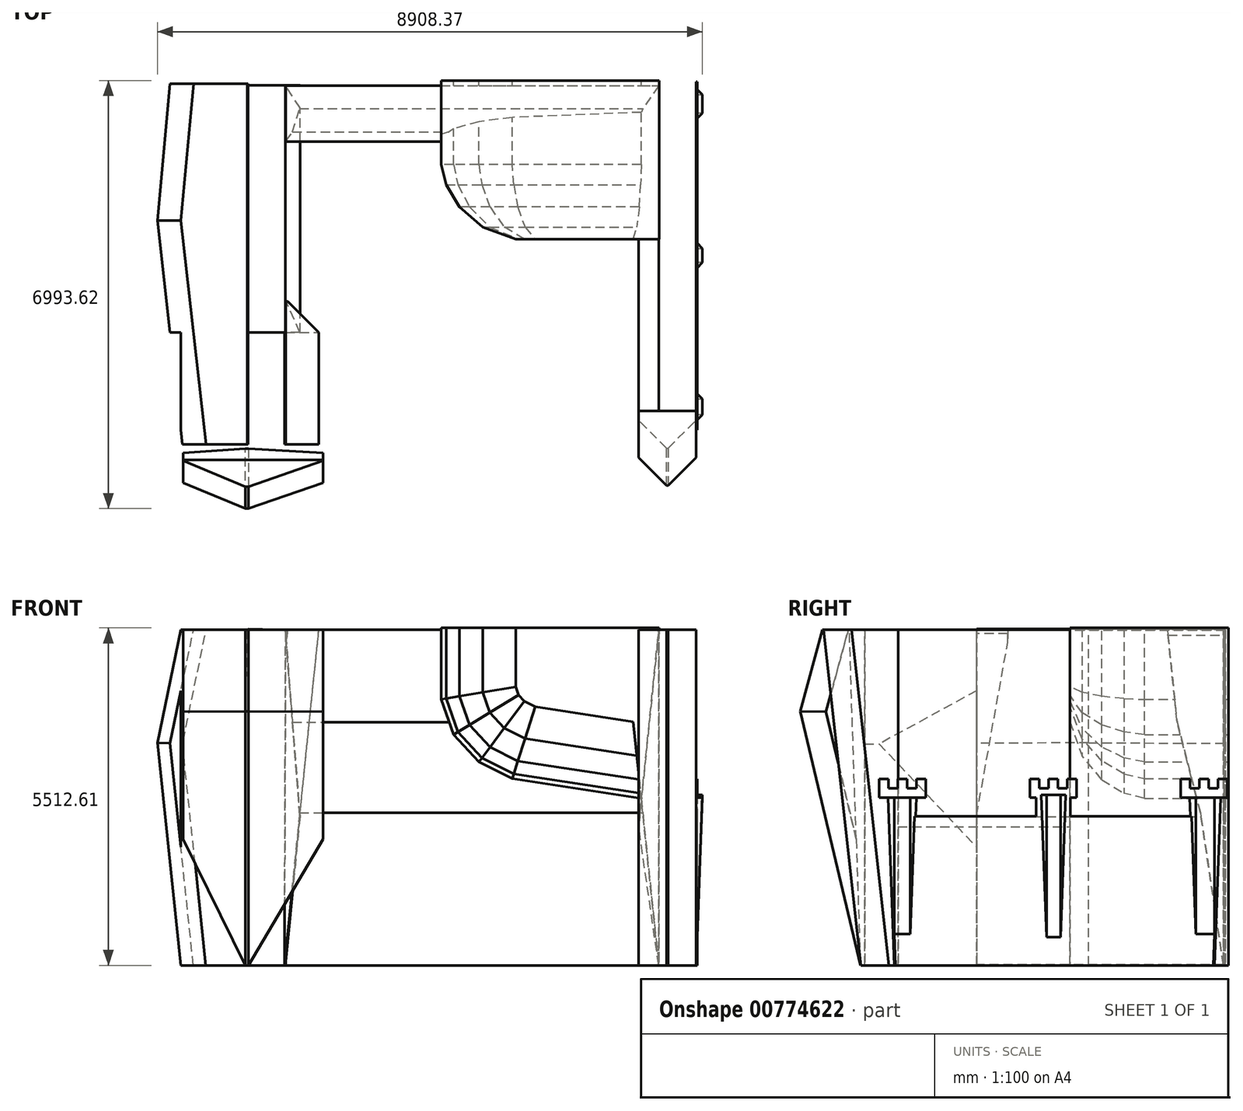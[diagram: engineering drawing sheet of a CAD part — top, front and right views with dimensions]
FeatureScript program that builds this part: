
annotation { "Feature Type Name" : "Feature", "Feature Type Description" : "" }
export const myFeature = defineFeature(function(context is Context, id is Id, definition is map)
    precondition{}
    {
        {
            var Q0;
            Q0=qCreatedBy(makeId("Right.planeOp"),FACE);
            var sketch = newSketch(context, id + "F0", { "sketchPlane" : qUnion([Q0])});
            skLineSegment(sketch, "E0", {"start": v(336.19, 0) * mm, "end": v(336.19, 2438.4) * mm});
            skLineSegment(sketch, "E1", {"start": v(336.19, 2438.4) * mm, "end": v(-5150.21, 2438.4) * mm});
            skLineSegment(sketch, "E2", {"start": v(-5150.21, 2438.4) * mm, "end": v(-5150.21, 0) * mm});
            skLineSegment(sketch, "E3", {"start": v(-5150.21, 0) * mm, "end": v(336.19, 0) * mm});
            skLineSegment(sketch, "E4", {"start": v(-5150.21, 2438.4) * mm, "end": v(-5150.21, 2743.2) * mm});
            skLineSegment(sketch, "E5", {"start": v(-5150.21, 2743.2) * mm, "end": v(-5251.81, 2743.2) * mm});
            skLineSegment(sketch, "E6", {"start": v(-5251.81, 2743.2) * mm, "end": v(-5251.81, 3048) * mm});
            skLineSegment(sketch, "E7", {"start": v(-5251.81, 3048) * mm, "end": v(-5099.41, 3048) * mm});
            skLineSegment(sketch, "E8", {"start": v(-5099.41, 3048) * mm, "end": v(-5099.41, 2895.6) * mm});
            skLineSegment(sketch, "E9", {"start": v(-5099.41, 2895.6) * mm, "end": v(-4947.01, 2895.6) * mm});
            skLineSegment(sketch, "E10", {"start": v(-4947.01, 2895.6) * mm, "end": v(-4947.01, 3048) * mm});
            skLineSegment(sketch, "E11", {"start": v(-4947.01, 3048) * mm, "end": v(-4794.61, 3048) * mm});
            skLineSegment(sketch, "E12", {"start": v(-4794.61, 3048) * mm, "end": v(-4794.61, 2895.6) * mm});
            skLineSegment(sketch, "E13", {"start": v(-4794.61, 2895.6) * mm, "end": v(-4642.21, 2895.6) * mm});
            skLineSegment(sketch, "E14", {"start": v(-4642.21, 2895.6) * mm, "end": v(-4642.21, 3048) * mm});
            skLineSegment(sketch, "E15", {"start": v(-4642.21, 3048) * mm, "end": v(-4489.81, 3048) * mm});
            skLineSegment(sketch, "E16", {"start": v(-4489.81, 3048) * mm, "end": v(-4489.81, 2743.2) * mm});
            skLineSegment(sketch, "E17", {"start": v(-4489.81, 2743.2) * mm, "end": v(-4591.41, 2743.2) * mm});
            skLineSegment(sketch, "E18", {"start": v(-4591.41, 2743.2) * mm, "end": v(-4591.41, 2438.4) * mm});
            skLineSegment(sketch, "E19", {"start": v(-4591.41, 2438.4) * mm, "end": v(-2686.41, 2438.4) * mm});
            skLineSegment(sketch, "E20", {"start": v(336.19, 2438.4) * mm, "end": v(336.19, 2743.2) * mm});
            skLineSegment(sketch, "E21", {"start": v(336.19, 2743.2) * mm, "end": v(437.79, 2743.2) * mm});
            skLineSegment(sketch, "E22", {"start": v(437.79, 2743.2) * mm, "end": v(437.79, 3048) * mm});
            skLineSegment(sketch, "E23", {"start": v(437.79, 3048) * mm, "end": v(285.39, 3048) * mm});
            skLineSegment(sketch, "E24", {"start": v(285.39, 3048) * mm, "end": v(285.39, 2895.6) * mm});
            skLineSegment(sketch, "E25", {"start": v(285.39, 2895.6) * mm, "end": v(132.99, 2895.6) * mm});
            skLineSegment(sketch, "E26", {"start": v(132.99, 2895.6) * mm, "end": v(132.99, 3048) * mm});
            skLineSegment(sketch, "E27", {"start": v(132.99, 3048) * mm, "end": v(-19.41, 3048) * mm});
            skLineSegment(sketch, "E28", {"start": v(-19.41, 3048) * mm, "end": v(-19.41, 2895.6) * mm});
            skLineSegment(sketch, "E29", {"start": v(-19.41, 2895.6) * mm, "end": v(-171.81, 2895.6) * mm});
            skLineSegment(sketch, "E30", {"start": v(-171.81, 2895.6) * mm, "end": v(-171.81, 3048) * mm});
            skLineSegment(sketch, "E31", {"start": v(-171.81, 3048) * mm, "end": v(-324.21, 3048) * mm});
            skLineSegment(sketch, "E32", {"start": v(-324.21, 3048) * mm, "end": v(-324.21, 2743.2) * mm});
            skLineSegment(sketch, "E33", {"start": v(-324.21, 2743.2) * mm, "end": v(-222.61, 2743.2) * mm});
            skLineSegment(sketch, "E34", {"start": v(-222.61, 2743.2) * mm, "end": v(-222.61, 2438.4) * mm});
            skLineSegment(sketch, "E35", {"start": v(-222.61, 2438.4) * mm, "end": v(-2127.61, 2438.4) * mm});
            skLineSegment(sketch, "E36", {"start": v(-2686.41, 2438.4) * mm, "end": v(-2686.41, 2743.2) * mm});
            skLineSegment(sketch, "E37", {"start": v(-2686.41, 2743.2) * mm, "end": v(-2788.01, 2743.2) * mm});
            skLineSegment(sketch, "E38", {"start": v(-2788.01, 2743.2) * mm, "end": v(-2788.01, 3048) * mm});
            skLineSegment(sketch, "E39", {"start": v(-2788.01, 3048) * mm, "end": v(-2635.61, 3048) * mm});
            skLineSegment(sketch, "E40", {"start": v(-2635.61, 3048) * mm, "end": v(-2635.61, 2895.6) * mm});
            skLineSegment(sketch, "E41", {"start": v(-2635.61, 2895.6) * mm, "end": v(-2483.21, 2895.6) * mm});
            skLineSegment(sketch, "E42", {"start": v(-2483.21, 2895.6) * mm, "end": v(-2483.21, 3048) * mm});
            skLineSegment(sketch, "E43", {"start": v(-2483.21, 3048) * mm, "end": v(-2330.81, 3048) * mm});
            skLineSegment(sketch, "E44", {"start": v(-2330.81, 3048) * mm, "end": v(-2330.81, 2895.6) * mm});
            skLineSegment(sketch, "E45", {"start": v(-2330.81, 2895.6) * mm, "end": v(-2178.41, 2895.6) * mm});
            skLineSegment(sketch, "E46", {"start": v(-2178.41, 2895.6) * mm, "end": v(-2178.41, 3048) * mm});
            skLineSegment(sketch, "E47", {"start": v(-2178.41, 3048) * mm, "end": v(-2026.01, 3048) * mm});
            skLineSegment(sketch, "E48", {"start": v(-2026.01, 3048) * mm, "end": v(-2026.01, 2743.2) * mm});
            skLineSegment(sketch, "E49", {"start": v(-2026.01, 2743.2) * mm, "end": v(-2127.61, 2743.2) * mm});
            skLineSegment(sketch, "E50", {"start": v(-2127.61, 2743.2) * mm, "end": v(-2127.61, 2438.4) * mm});
            skLineSegment(sketch, "E51", {"start": v(-2127.61, 2438.4) * mm, "end": v(-2127.61, 2438.4) * mm});
            skLineSegment(sketch, "E52", {"start": v(-2127.61, 2438.4) * mm, "end": v(-2686.41, 2438.4) * mm});
            skSolve(sketch);
        }
        {
            var Q0;
            Q0 = qSketchRegion(id + "F0", true);
            extrude(context, id + "F1", {"entities" : qUnion([Q0]), "depth" : 19.05 * mm, "offsetDistance" : 25.4 * mm});
        }
        {
            var Q0;
            Q0=qCreatedBy(makeId("Front.planeOp"),FACE);
            var sketch = newSketch(context, id + "F2", { "sketchPlane" : qUnion([Q0])});
            skLineSegment(sketch, "E53", {"start": v(0, 0) * mm, "end": v(0, 2743.2) * mm});
            skLineSegment(sketch, "E54", {"start": v(0, 2743.2) * mm, "end": v(101.6, 2743.2) * mm});
            skLineSegment(sketch, "E55", {"start": v(101.6, 2743.2) * mm, "end": v(0, 0) * mm});
            skSolve(sketch);
        }
        {
            var Q0;
            Q0 = qSketchRegion(id + "F2", true);
            extrude(context, id + "F3", {"entities" : qUnion([Q0]), "operationType" : NewBodyOperationType.ADD, "depth" : 228.6 * mm, "offsetDistance" : 25.4 * mm, "hasSecondDirection" : true, "secondDirectionOppositeDirection" : true, "secondDirectionDepth" : 381 * mm});
        }
        {
            var Q0;
            Q0=makeQuery(id+"F3.opExtrude","CAP_EDGE",EDGE,{"disambiguationData":[OSD([sQuery(id+"F2.wireOp",EDGE,"E55")])],"isStart":false});
            var Q1;
            Q1=makeQuery(id+"F3.opExtrude","CAP_EDGE",EDGE,{"disambiguationData":[OSD([sQuery(id+"F2.wireOp",EDGE,"E55")])],"isStart":true});
            chamfer(context, id + "F4", {"entities" : qUnion([Q0, Q1]), "width" : 152.4 * mm, "tangentPropagation" : true});
        }
        {
            var Q0;
            Q0=qCreatedBy(makeId("Front.planeOp"),FACE);
            var sketch = newSketch(context, id + "F5", { "sketchPlane" : qUnion([Q0])});
            skLineSegment(sketch, "E56", {"start": v(3.6, 45.14) * mm, "end": v(3.6, 2788.34) * mm});
            skLineSegment(sketch, "E57", {"start": v(3.6, 2788.34) * mm, "end": v(105.2, 2788.34) * mm});
            skLineSegment(sketch, "E58", {"start": v(105.2, 2788.34) * mm, "end": v(3.6, 45.14) * mm});
            skSolve(sketch);
        }
        {
            var Q0;
            Q0 = qSketchRegion(id + "F5", true);
            extrude(context, id + "F6", {"entities" : qUnion([Q0]), "operationType" : NewBodyOperationType.ADD, "depth" : 2667 * mm, "offsetDistance" : 25.4 * mm, "hasSecondDirection" : true, "secondDirectionOppositeDirection" : false, "secondDirectionDepth" : 2133.6 * mm});
        }
        {
            var Q0;
            Q0=makeQuery(id+"F6.opExtrude","CAP_EDGE",EDGE,{"disambiguationData":[OSD([sQuery(id+"F5.wireOp",EDGE,"E58")])],"isStart":true});
            var Q1;
            Q1=makeQuery(id+"F6.opExtrude","CAP_EDGE",EDGE,{"disambiguationData":[OSD([sQuery(id+"F5.wireOp",EDGE,"E58")])],"isStart":false});
            chamfer(context, id + "F7", {"entities" : qUnion([Q0, Q1]), "width" : 152.4 * mm, "tangentPropagation" : true});
        }
        {
            var Q0;
            Q0=qCreatedBy(makeId("Front.planeOp"),FACE);
            var sketch = newSketch(context, id + "F8", { "sketchPlane" : qUnion([Q0])});
            skLineSegment(sketch, "E59", {"start": v(0, 0) * mm, "end": v(0, 2743.2) * mm});
            skLineSegment(sketch, "E60", {"start": v(0, 2743.2) * mm, "end": v(101.6, 2743.2) * mm});
            skLineSegment(sketch, "E61", {"start": v(101.6, 2743.2) * mm, "end": v(0, 0) * mm});
            skSolve(sketch);
        }
        {
            var Q0;
            Q0 = qSketchRegion(id + "F8", true);
            extrude(context, id + "F9", {"entities" : qUnion([Q0]), "operationType" : NewBodyOperationType.ADD, "depth" : 5156.2 * mm, "offsetDistance" : 25.4 * mm, "hasSecondDirection" : true, "secondDirectionOppositeDirection" : false, "secondDirectionDepth" : 4589.78 * mm});
        }
        {
            var Q0;
            Q0=makeQuery(id+"F9.opExtrude","CAP_EDGE",EDGE,{"disambiguationData":[OSD([sQuery(id+"F8.wireOp",EDGE,"E61")])],"isStart":false});
            var Q1;
            Q1=makeQuery(id+"F9.opExtrude","CAP_EDGE",EDGE,{"disambiguationData":[OSD([sQuery(id+"F8.wireOp",EDGE,"E61")])],"isStart":true});
            chamfer(context, id + "F10", {"entities" : qUnion([Q0, Q1]), "width" : 152.4 * mm, "tangentPropagation" : true});
        }
        {
            var Q0;
            Q0=qCreatedBy(makeId("Front.planeOp"),FACE);
            var sketch = newSketch(context, id + "F11", { "sketchPlane" : qUnion([Q0])});
            skLineSegment(sketch, "E62", {"start": v(0, 0) * mm, "end": v(-609.6, 0) * mm});
            skLineSegment(sketch, "E63", {"start": v(-609.6, 0) * mm, "end": v(-609.6, 5486.4) * mm});
            skLineSegment(sketch, "E64", {"start": v(-609.6, 0) * mm, "end": v(-938.3, 2262.25) * mm});
            skLineSegment(sketch, "E65", {"start": v(-938.3, 2262.25) * mm, "end": v(-609.6, 5486.4) * mm});
            skSolve(sketch);
        }
        {
            var Q0;
            Q0 = qSketchRegion(id + "F11", true);
            extrude(context, id + "F12", {"entities" : qUnion([Q0]), "depth" : 4978.4 * mm, "offsetDistance" : 25.4 * mm, "hasSecondDirection" : true, "secondDirectionOppositeDirection" : false, "secondDirectionDepth" : 2133.6 * mm});
        }
        {
            var Q0;
            Q0=qCreatedBy(makeId("Front.planeOp"),FACE);
            var sketch = newSketch(context, id + "F13", { "sketchPlane" : qUnion([Q0])});
            skLineSegment(sketch, "E66", {"start": v(-608.8, 0) * mm, "end": v(-895.68, 2728.16) * mm});
            skLineSegment(sketch, "E67", {"start": v(-895.68, 2728.16) * mm, "end": v(-3004.94, 3049.56) * mm});
            skLineSegment(sketch, "E68", {"start": v(-3004.94, 3049.56) * mm, "end": v(-3549.82, 3322.9) * mm});
            skLineSegment(sketch, "E69", {"start": v(-3549.82, 3322.9) * mm, "end": v(-3964.79, 3769.46) * mm});
            skLineSegment(sketch, "E70", {"start": v(-3964.79, 3769.46) * mm, "end": v(-4167.95, 4344.2) * mm});
            skLineSegment(sketch, "E71", {"start": v(-4167.95, 4344.2) * mm, "end": v(-4167.95, 5512.6) * mm});
            skLineSegment(sketch, "E72", {"start": v(-4167.95, 5512.6) * mm, "end": v(-605.67, 5512.6) * mm});
            skLineSegment(sketch, "E73", {"start": v(-605.67, 5512.6) * mm, "end": v(-608.8, 0) * mm});
            skSolve(sketch);
        }
        {
            var Q0;
            Q0 = qSketchRegion(id + "F13", true);
            extrude(context, id + "F14", {"entities" : qUnion([Q0]), "operationType" : NewBodyOperationType.ADD, "depth" : 2133.6 * mm, "offsetDistance" : 25.4 * mm, "hasSecondDirection" : true, "secondDirectionOppositeDirection" : true, "secondDirectionDepth" : 457.2 * mm});
        }
        {
            var Q0;
            Q0=makeQuery(id+"F14.opExtrude","CAP_EDGE",EDGE,{"disambiguationData":[OSD([sQuery(id+"F13.wireOp",EDGE,"E70")])],"isStart":false});
            var Q1;
            Q1=makeQuery(id+"F14.opExtrude","CAP_EDGE",EDGE,{"disambiguationData":[OSD([sQuery(id+"F13.wireOp",EDGE,"E71")])],"isStart":false});
            var Q2;
            Q2=makeQuery(id+"F14.opExtrude","CAP_EDGE",EDGE,{"disambiguationData":[OSD([sQuery(id+"F13.wireOp",EDGE,"E69")])],"isStart":false});
            var Q3;
            Q3=makeQuery(id+"F14.opExtrude","CAP_EDGE",EDGE,{"disambiguationData":[OSD([sQuery(id+"F13.wireOp",EDGE,"E67")])],"isStart":false});
            var Q4;
            Q4=makeQuery(id+"F14.opExtrude","CAP_EDGE",EDGE,{"disambiguationData":[OSD([sQuery(id+"F13.wireOp",EDGE,"E68")])],"isStart":false});
            chamfer(context, id + "F15", {"entities" : qUnion([Q0, Q1, Q2, Q3, Q4]), "chamferType" : ChamferType.TWO_OFFSETS, "width1" : 1219.2 * mm, "oppositeDirection" : false, "width2" : 304.8 * mm, "tangentPropagation" : true});
        }
        {
            var Q0;
            {var subQ0=sQuery(id+"F13.wireOp",EDGE,"E71");Q0=makeQuery(id+"F15.opChamfer","BLEND_EDGE",EDGE,{"blendedFrom":[makeQuery(id+"F14.opExtrude","CAP_EDGE",EDGE,{"disambiguationData":[OSD([subQ0])],"isStart":false}),makeQuery(id+"F14.opExtrude","CAP_FACE",FACE,{"disambiguationData":[OSD([sQuery(id+"F13.wireOp",EDGE,"E66"),sQuery(id+"F13.wireOp",EDGE,"E67"),sQuery(id+"F13.wireOp",EDGE,"E68"),sQuery(id+"F13.wireOp",EDGE,"E69"),sQuery(id+"F13.wireOp",EDGE,"E70"),subQ0,sQuery(id+"F13.wireOp",EDGE,"E72"),sQuery(id+"F13.wireOp",EDGE,"E73")])],"isStart":false})],"blendedInto":[makeQuery(id+"F14.opExtrude","CAP_FACE",FACE,{"disambiguationData":[OSD([sQuery(id+"F13.wireOp",EDGE,"E66"),sQuery(id+"F13.wireOp",EDGE,"E67"),sQuery(id+"F13.wireOp",EDGE,"E68"),sQuery(id+"F13.wireOp",EDGE,"E69"),sQuery(id+"F13.wireOp",EDGE,"E70"),subQ0,sQuery(id+"F13.wireOp",EDGE,"E72"),sQuery(id+"F13.wireOp",EDGE,"E73")])],"isStart":false})]});}
            var Q1;
            {var subQ0=sQuery(id+"F13.wireOp",EDGE,"E70");Q1=makeQuery(id+"F15.opChamfer","BLEND_EDGE",EDGE,{"blendedFrom":[makeQuery(id+"F14.opExtrude","CAP_EDGE",EDGE,{"disambiguationData":[OSD([subQ0])],"isStart":false}),makeQuery(id+"F14.opExtrude","CAP_FACE",FACE,{"disambiguationData":[OSD([sQuery(id+"F13.wireOp",EDGE,"E66"),sQuery(id+"F13.wireOp",EDGE,"E67"),sQuery(id+"F13.wireOp",EDGE,"E68"),sQuery(id+"F13.wireOp",EDGE,"E69"),subQ0,sQuery(id+"F13.wireOp",EDGE,"E71"),sQuery(id+"F13.wireOp",EDGE,"E72"),sQuery(id+"F13.wireOp",EDGE,"E73")])],"isStart":false})],"blendedInto":[makeQuery(id+"F14.opExtrude","CAP_FACE",FACE,{"disambiguationData":[OSD([sQuery(id+"F13.wireOp",EDGE,"E66"),sQuery(id+"F13.wireOp",EDGE,"E67"),sQuery(id+"F13.wireOp",EDGE,"E68"),sQuery(id+"F13.wireOp",EDGE,"E69"),subQ0,sQuery(id+"F13.wireOp",EDGE,"E71"),sQuery(id+"F13.wireOp",EDGE,"E72"),sQuery(id+"F13.wireOp",EDGE,"E73")])],"isStart":false})]});}
            var Q2;
            {var subQ0=sQuery(id+"F13.wireOp",EDGE,"E69");Q2=makeQuery(id+"F15.opChamfer","BLEND_EDGE",EDGE,{"blendedFrom":[makeQuery(id+"F14.opExtrude","CAP_EDGE",EDGE,{"disambiguationData":[OSD([subQ0])],"isStart":false}),makeQuery(id+"F14.opExtrude","CAP_FACE",FACE,{"disambiguationData":[OSD([sQuery(id+"F13.wireOp",EDGE,"E66"),sQuery(id+"F13.wireOp",EDGE,"E67"),sQuery(id+"F13.wireOp",EDGE,"E68"),subQ0,sQuery(id+"F13.wireOp",EDGE,"E70"),sQuery(id+"F13.wireOp",EDGE,"E71"),sQuery(id+"F13.wireOp",EDGE,"E72"),sQuery(id+"F13.wireOp",EDGE,"E73")])],"isStart":false})],"blendedInto":[makeQuery(id+"F14.opExtrude","CAP_FACE",FACE,{"disambiguationData":[OSD([sQuery(id+"F13.wireOp",EDGE,"E66"),sQuery(id+"F13.wireOp",EDGE,"E67"),sQuery(id+"F13.wireOp",EDGE,"E68"),subQ0,sQuery(id+"F13.wireOp",EDGE,"E70"),sQuery(id+"F13.wireOp",EDGE,"E71"),sQuery(id+"F13.wireOp",EDGE,"E72"),sQuery(id+"F13.wireOp",EDGE,"E73")])],"isStart":false})]});}
            var Q3;
            {var subQ0=sQuery(id+"F13.wireOp",EDGE,"E68");Q3=makeQuery(id+"F15.opChamfer","BLEND_EDGE",EDGE,{"blendedFrom":[makeQuery(id+"F14.opExtrude","CAP_EDGE",EDGE,{"disambiguationData":[OSD([subQ0])],"isStart":false}),makeQuery(id+"F14.opExtrude","CAP_FACE",FACE,{"disambiguationData":[OSD([sQuery(id+"F13.wireOp",EDGE,"E66"),sQuery(id+"F13.wireOp",EDGE,"E67"),subQ0,sQuery(id+"F13.wireOp",EDGE,"E69"),sQuery(id+"F13.wireOp",EDGE,"E70"),sQuery(id+"F13.wireOp",EDGE,"E71"),sQuery(id+"F13.wireOp",EDGE,"E72"),sQuery(id+"F13.wireOp",EDGE,"E73")])],"isStart":false})],"blendedInto":[makeQuery(id+"F14.opExtrude","CAP_FACE",FACE,{"disambiguationData":[OSD([sQuery(id+"F13.wireOp",EDGE,"E66"),sQuery(id+"F13.wireOp",EDGE,"E67"),subQ0,sQuery(id+"F13.wireOp",EDGE,"E69"),sQuery(id+"F13.wireOp",EDGE,"E70"),sQuery(id+"F13.wireOp",EDGE,"E71"),sQuery(id+"F13.wireOp",EDGE,"E72"),sQuery(id+"F13.wireOp",EDGE,"E73")])],"isStart":false})]});}
            var Q4;
            {var subQ0=sQuery(id+"F13.wireOp",EDGE,"E67");Q4=makeQuery(id+"F15.opChamfer","BLEND_EDGE",EDGE,{"blendedFrom":[makeQuery(id+"F14.opExtrude","CAP_EDGE",EDGE,{"disambiguationData":[OSD([subQ0])],"isStart":false}),makeQuery(id+"F14.opExtrude","CAP_FACE",FACE,{"disambiguationData":[OSD([sQuery(id+"F13.wireOp",EDGE,"E66"),subQ0,sQuery(id+"F13.wireOp",EDGE,"E68"),sQuery(id+"F13.wireOp",EDGE,"E69"),sQuery(id+"F13.wireOp",EDGE,"E70"),sQuery(id+"F13.wireOp",EDGE,"E71"),sQuery(id+"F13.wireOp",EDGE,"E72"),sQuery(id+"F13.wireOp",EDGE,"E73")])],"isStart":false})],"blendedInto":[makeQuery(id+"F14.opExtrude","CAP_FACE",FACE,{"disambiguationData":[OSD([sQuery(id+"F13.wireOp",EDGE,"E66"),subQ0,sQuery(id+"F13.wireOp",EDGE,"E68"),sQuery(id+"F13.wireOp",EDGE,"E69"),sQuery(id+"F13.wireOp",EDGE,"E70"),sQuery(id+"F13.wireOp",EDGE,"E71"),sQuery(id+"F13.wireOp",EDGE,"E72"),sQuery(id+"F13.wireOp",EDGE,"E73")])],"isStart":false})]});}
            chamfer(context, id + "F16", {"entities" : qUnion([Q0, Q1, Q2, Q3, Q4]), "chamferType" : ChamferType.TWO_OFFSETS, "width1" : 304.8 * mm, "oppositeDirection" : false, "width2" : 914.4 * mm, "tangentPropagation" : true});
        }
        {
            var Q0;
            {var subQ0=sQuery(id+"F13.wireOp",EDGE,"E71");var subQ1=makeQuery(id+"F14.opExtrude","CAP_FACE",FACE,{"disambiguationData":[OSD([sQuery(id+"F13.wireOp",EDGE,"E66"),sQuery(id+"F13.wireOp",EDGE,"E67"),sQuery(id+"F13.wireOp",EDGE,"E68"),sQuery(id+"F13.wireOp",EDGE,"E69"),sQuery(id+"F13.wireOp",EDGE,"E70"),subQ0,sQuery(id+"F13.wireOp",EDGE,"E72"),sQuery(id+"F13.wireOp",EDGE,"E73")])],"isStart":false});Q0=makeQuery(id+"F16.opChamfer","BLEND_EDGE",EDGE,{"blendedFrom":[makeQuery(id+"F15.opChamfer","BLEND_EDGE",EDGE,{"blendedFrom":[makeQuery(id+"F14.opExtrude","CAP_EDGE",EDGE,{"disambiguationData":[OSD([subQ0])],"isStart":false}),subQ1],"blendedInto":[subQ1]}),subQ1],"blendedInto":[subQ1]});}
            var Q1;
            {var subQ0=sQuery(id+"F13.wireOp",EDGE,"E70");var subQ1=makeQuery(id+"F14.opExtrude","CAP_FACE",FACE,{"disambiguationData":[OSD([sQuery(id+"F13.wireOp",EDGE,"E66"),sQuery(id+"F13.wireOp",EDGE,"E67"),sQuery(id+"F13.wireOp",EDGE,"E68"),sQuery(id+"F13.wireOp",EDGE,"E69"),subQ0,sQuery(id+"F13.wireOp",EDGE,"E71"),sQuery(id+"F13.wireOp",EDGE,"E72"),sQuery(id+"F13.wireOp",EDGE,"E73")])],"isStart":false});Q1=makeQuery(id+"F16.opChamfer","BLEND_EDGE",EDGE,{"blendedFrom":[makeQuery(id+"F15.opChamfer","BLEND_EDGE",EDGE,{"blendedFrom":[makeQuery(id+"F14.opExtrude","CAP_EDGE",EDGE,{"disambiguationData":[OSD([subQ0])],"isStart":false}),subQ1],"blendedInto":[subQ1]}),subQ1],"blendedInto":[subQ1]});}
            var Q2;
            {var subQ0=sQuery(id+"F13.wireOp",EDGE,"E69");var subQ1=makeQuery(id+"F14.opExtrude","CAP_FACE",FACE,{"disambiguationData":[OSD([sQuery(id+"F13.wireOp",EDGE,"E66"),sQuery(id+"F13.wireOp",EDGE,"E67"),sQuery(id+"F13.wireOp",EDGE,"E68"),subQ0,sQuery(id+"F13.wireOp",EDGE,"E70"),sQuery(id+"F13.wireOp",EDGE,"E71"),sQuery(id+"F13.wireOp",EDGE,"E72"),sQuery(id+"F13.wireOp",EDGE,"E73")])],"isStart":false});Q2=makeQuery(id+"F16.opChamfer","BLEND_EDGE",EDGE,{"blendedFrom":[makeQuery(id+"F15.opChamfer","BLEND_EDGE",EDGE,{"blendedFrom":[makeQuery(id+"F14.opExtrude","CAP_EDGE",EDGE,{"disambiguationData":[OSD([subQ0])],"isStart":false}),subQ1],"blendedInto":[subQ1]}),subQ1],"blendedInto":[subQ1]});}
            var Q3;
            {var subQ0=sQuery(id+"F13.wireOp",EDGE,"E68");var subQ1=makeQuery(id+"F14.opExtrude","CAP_FACE",FACE,{"disambiguationData":[OSD([sQuery(id+"F13.wireOp",EDGE,"E66"),sQuery(id+"F13.wireOp",EDGE,"E67"),subQ0,sQuery(id+"F13.wireOp",EDGE,"E69"),sQuery(id+"F13.wireOp",EDGE,"E70"),sQuery(id+"F13.wireOp",EDGE,"E71"),sQuery(id+"F13.wireOp",EDGE,"E72"),sQuery(id+"F13.wireOp",EDGE,"E73")])],"isStart":false});Q3=makeQuery(id+"F16.opChamfer","BLEND_EDGE",EDGE,{"blendedFrom":[makeQuery(id+"F15.opChamfer","BLEND_EDGE",EDGE,{"blendedFrom":[makeQuery(id+"F14.opExtrude","CAP_EDGE",EDGE,{"disambiguationData":[OSD([subQ0])],"isStart":false}),subQ1],"blendedInto":[subQ1]}),subQ1],"blendedInto":[subQ1]});}
            var Q4;
            {var subQ0=sQuery(id+"F13.wireOp",EDGE,"E67");var subQ1=makeQuery(id+"F14.opExtrude","CAP_FACE",FACE,{"disambiguationData":[OSD([sQuery(id+"F13.wireOp",EDGE,"E66"),subQ0,sQuery(id+"F13.wireOp",EDGE,"E68"),sQuery(id+"F13.wireOp",EDGE,"E69"),sQuery(id+"F13.wireOp",EDGE,"E70"),sQuery(id+"F13.wireOp",EDGE,"E71"),sQuery(id+"F13.wireOp",EDGE,"E72"),sQuery(id+"F13.wireOp",EDGE,"E73")])],"isStart":false});Q4=makeQuery(id+"F16.opChamfer","BLEND_EDGE",EDGE,{"blendedFrom":[makeQuery(id+"F15.opChamfer","BLEND_EDGE",EDGE,{"blendedFrom":[makeQuery(id+"F14.opExtrude","CAP_EDGE",EDGE,{"disambiguationData":[OSD([subQ0])],"isStart":false}),subQ1],"blendedInto":[subQ1]}),subQ1],"blendedInto":[subQ1]});}
            chamfer(context, id + "F17", {"entities" : qUnion([Q0, Q1, Q2, Q3, Q4]), "chamferType" : ChamferType.TWO_OFFSETS, "width1" : 304.8 * mm, "oppositeDirection" : false, "width2" : 609.6 * mm, "tangentPropagation" : true});
        }
        {
            var Q0;
            {var subQ0=sQuery(id+"F13.wireOp",EDGE,"E71");var subQ1=makeQuery(id+"F14.opExtrude","CAP_FACE",FACE,{"disambiguationData":[OSD([sQuery(id+"F13.wireOp",EDGE,"E66"),sQuery(id+"F13.wireOp",EDGE,"E67"),sQuery(id+"F13.wireOp",EDGE,"E68"),sQuery(id+"F13.wireOp",EDGE,"E69"),sQuery(id+"F13.wireOp",EDGE,"E70"),subQ0,sQuery(id+"F13.wireOp",EDGE,"E72"),sQuery(id+"F13.wireOp",EDGE,"E73")])],"isStart":false});var subQ2=subQ1;Q0=makeQuery(id+"F17.opChamfer","BLEND_EDGE",EDGE,{"blendedFrom":[makeQuery(id+"F16.opChamfer","BLEND_EDGE",EDGE,{"blendedFrom":[makeQuery(id+"F15.opChamfer","BLEND_EDGE",EDGE,{"blendedFrom":[makeQuery(id+"F14.opExtrude","CAP_EDGE",EDGE,{"disambiguationData":[OSD([subQ0])],"isStart":false}),subQ1],"blendedInto":[subQ1]}),subQ2],"blendedInto":[subQ2]}),subQ2],"blendedInto":[subQ2]});}
            var Q1;
            {var subQ0=sQuery(id+"F13.wireOp",EDGE,"E70");var subQ1=makeQuery(id+"F14.opExtrude","CAP_FACE",FACE,{"disambiguationData":[OSD([sQuery(id+"F13.wireOp",EDGE,"E66"),sQuery(id+"F13.wireOp",EDGE,"E67"),sQuery(id+"F13.wireOp",EDGE,"E68"),sQuery(id+"F13.wireOp",EDGE,"E69"),subQ0,sQuery(id+"F13.wireOp",EDGE,"E71"),sQuery(id+"F13.wireOp",EDGE,"E72"),sQuery(id+"F13.wireOp",EDGE,"E73")])],"isStart":false});var subQ2=subQ1;Q1=makeQuery(id+"F17.opChamfer","BLEND_EDGE",EDGE,{"blendedFrom":[makeQuery(id+"F16.opChamfer","BLEND_EDGE",EDGE,{"blendedFrom":[makeQuery(id+"F15.opChamfer","BLEND_EDGE",EDGE,{"blendedFrom":[makeQuery(id+"F14.opExtrude","CAP_EDGE",EDGE,{"disambiguationData":[OSD([subQ0])],"isStart":false}),subQ1],"blendedInto":[subQ1]}),subQ2],"blendedInto":[subQ2]}),subQ2],"blendedInto":[subQ2]});}
            var Q2;
            {var subQ0=sQuery(id+"F13.wireOp",EDGE,"E68");var subQ1=makeQuery(id+"F14.opExtrude","CAP_FACE",FACE,{"disambiguationData":[OSD([sQuery(id+"F13.wireOp",EDGE,"E66"),sQuery(id+"F13.wireOp",EDGE,"E67"),subQ0,sQuery(id+"F13.wireOp",EDGE,"E69"),sQuery(id+"F13.wireOp",EDGE,"E70"),sQuery(id+"F13.wireOp",EDGE,"E71"),sQuery(id+"F13.wireOp",EDGE,"E72"),sQuery(id+"F13.wireOp",EDGE,"E73")])],"isStart":false});var subQ2=subQ1;Q2=makeQuery(id+"F17.opChamfer","BLEND_EDGE",EDGE,{"blendedFrom":[makeQuery(id+"F16.opChamfer","BLEND_EDGE",EDGE,{"blendedFrom":[makeQuery(id+"F15.opChamfer","BLEND_EDGE",EDGE,{"blendedFrom":[makeQuery(id+"F14.opExtrude","CAP_EDGE",EDGE,{"disambiguationData":[OSD([subQ0])],"isStart":false}),subQ1],"blendedInto":[subQ1]}),subQ2],"blendedInto":[subQ2]}),subQ2],"blendedInto":[subQ2]});}
            var Q3;
            {var subQ0=sQuery(id+"F13.wireOp",EDGE,"E69");var subQ1=makeQuery(id+"F14.opExtrude","CAP_FACE",FACE,{"disambiguationData":[OSD([sQuery(id+"F13.wireOp",EDGE,"E66"),sQuery(id+"F13.wireOp",EDGE,"E67"),sQuery(id+"F13.wireOp",EDGE,"E68"),subQ0,sQuery(id+"F13.wireOp",EDGE,"E70"),sQuery(id+"F13.wireOp",EDGE,"E71"),sQuery(id+"F13.wireOp",EDGE,"E72"),sQuery(id+"F13.wireOp",EDGE,"E73")])],"isStart":false});var subQ2=subQ1;Q3=makeQuery(id+"F17.opChamfer","BLEND_EDGE",EDGE,{"blendedFrom":[makeQuery(id+"F16.opChamfer","BLEND_EDGE",EDGE,{"blendedFrom":[makeQuery(id+"F15.opChamfer","BLEND_EDGE",EDGE,{"blendedFrom":[makeQuery(id+"F14.opExtrude","CAP_EDGE",EDGE,{"disambiguationData":[OSD([subQ0])],"isStart":false}),subQ1],"blendedInto":[subQ1]}),subQ2],"blendedInto":[subQ2]}),subQ2],"blendedInto":[subQ2]});}
            var Q4;
            {var subQ0=sQuery(id+"F13.wireOp",EDGE,"E67");var subQ1=makeQuery(id+"F14.opExtrude","CAP_FACE",FACE,{"disambiguationData":[OSD([sQuery(id+"F13.wireOp",EDGE,"E66"),subQ0,sQuery(id+"F13.wireOp",EDGE,"E68"),sQuery(id+"F13.wireOp",EDGE,"E69"),sQuery(id+"F13.wireOp",EDGE,"E70"),sQuery(id+"F13.wireOp",EDGE,"E71"),sQuery(id+"F13.wireOp",EDGE,"E72"),sQuery(id+"F13.wireOp",EDGE,"E73")])],"isStart":false});var subQ2=subQ1;Q4=makeQuery(id+"F17.opChamfer","BLEND_EDGE",EDGE,{"blendedFrom":[makeQuery(id+"F16.opChamfer","BLEND_EDGE",EDGE,{"blendedFrom":[makeQuery(id+"F15.opChamfer","BLEND_EDGE",EDGE,{"blendedFrom":[makeQuery(id+"F14.opExtrude","CAP_EDGE",EDGE,{"disambiguationData":[OSD([subQ0])],"isStart":false}),subQ1],"blendedInto":[subQ1]}),subQ2],"blendedInto":[subQ2]}),subQ2],"blendedInto":[subQ2]});}
            chamfer(context, id + "F18", {"entities" : qUnion([Q0, Q1, Q2, Q3, Q4]), "chamferType" : ChamferType.TWO_OFFSETS, "width1" : 304.8 * mm, "oppositeDirection" : false, "width2" : 304.8 * mm, "tangentPropagation" : true});
        }
        {
            var Q0;
            Q0=qCreatedBy(makeId("Right.planeOp"),FACE);
            var sketch = newSketch(context, id + "F19", { "sketchPlane" : qUnion([Q0])});
            skLineSegment(sketch, "E74", {"start": v(-4940.36, 0) * mm, "end": v(-4940.36, 5486.4) * mm});
            skLineSegment(sketch, "E75", {"start": v(-4940.36, 5486.4) * mm, "end": v(-5549.96, 5486.4) * mm});
            skLineSegment(sketch, "E76", {"start": v(-5549.96, 0) * mm, "end": v(-4940.36, 0) * mm});
            skLineSegment(sketch, "E77", {"start": v(-5549.96, 5486.4) * mm, "end": v(-6159.56, 5486.4) * mm});
            skLineSegment(sketch, "E78", {"start": v(-6159.56, 5486.4) * mm, "end": v(-5549.96, 0) * mm});
            skSolve(sketch);
        }
        {
            var Q0;
            Q0 = qSketchRegion(id + "F19", true);
            extrude(context, id + "F20", {"entities" : qUnion([Q0]), "operationType" : NewBodyOperationType.ADD, "depth" : 0 * mm, "offsetDistance" : 25.4 * mm, "hasSecondDirection" : true, "secondDirectionOppositeDirection" : true, "secondDirectionDepth" : 939.8 * mm});
        }
        {
            var Q0;
            Q0=makeQuery(id+"F20.opExtrude","CAP_EDGE",EDGE,{"disambiguationData":[OSD([sQuery(id+"F19.wireOp",EDGE,"E78")])],"isStart":false});
            var Q1;
            Q1=makeQuery(id+"F20.opExtrude","CAP_EDGE",EDGE,{"disambiguationData":[OSD([sQuery(id+"F19.wireOp",EDGE,"E78")])],"isStart":true});
            chamfer(context, id + "F21", {"entities" : qUnion([Q0, Q1]), "width" : 457.2 * mm, "tangentPropagation" : true});
        }
        {
            var Q0;
            Q0=qCreatedBy(makeId("Right.planeOp"),FACE);
            var sketch = newSketch(context, id + "F22", { "sketchPlane" : qUnion([Q0])});
            skLineSegment(sketch, "E79", {"start": v(374.8, 0) * mm, "end": v(374.8, 5486.4) * mm});
            skLineSegment(sketch, "E80", {"start": v(374.8, 5486.4) * mm, "end": v(-539.6, 5486.4) * mm});
            skLineSegment(sketch, "E81", {"start": v(-539.6, 5486.4) * mm, "end": v(-381.75, 3970.6) * mm});
            skLineSegment(sketch, "E82", {"start": v(-381.75, 3970.6) * mm, "end": v(0, 2495.18) * mm});
            skLineSegment(sketch, "E83", {"start": v(0, 2495.18) * mm, "end": v(374.8, 0) * mm});
            skSolve(sketch);
        }
        {
            var Q0;
            Q0 = qSketchRegion(id + "F22", true);
            extrude(context, id + "F23", {"entities" : qUnion([Q0]), "operationType" : NewBodyOperationType.ADD, "oppositeDirection" : true, "depth" : 6705.6 * mm, "offsetDistance" : 25.4 * mm, "hasSecondDirection" : true, "secondDirectionOppositeDirection" : true, "secondDirectionDepth" : 609.6 * mm});
        }
        {
            var Q0;
            Q0=qCreatedBy(makeId("Front.planeOp"),FACE);
            var sketch = newSketch(context, id + "F24", { "sketchPlane" : qUnion([Q0])});
            skLineSegment(sketch, "E84", {"start": v(-6711.86, 0) * mm, "end": v(-6473.24, 2426.7) * mm});
            skLineSegment(sketch, "E85", {"start": v(-6473.24, 2426.7) * mm, "end": v(-6712.04, 5480.02) * mm});
            skLineSegment(sketch, "E86", {"start": v(-6712.04, 5480.02) * mm, "end": v(-7321.46, 5495.04) * mm});
            skLineSegment(sketch, "E87", {"start": v(-7321.46, 5495.04) * mm, "end": v(-7321.46, 0) * mm});
            skLineSegment(sketch, "E88", {"start": v(-7321.46, 0) * mm, "end": v(-6711.86, 0) * mm});
            skLineSegment(sketch, "E89", {"start": v(-6711.86, 0) * mm, "end": v(-6712.04, 5480.02) * mm});
            skSolve(sketch);
        }
        {
            var Q0;
            Q0 = qSketchRegion(id + "F24", true);
            extrude(context, id + "F25", {"entities" : qUnion([Q0]), "operationType" : NewBodyOperationType.ADD, "depth" : 3657.6 * mm, "offsetDistance" : 25.4 * mm, "hasSecondDirection" : true, "secondDirectionOppositeDirection" : true, "secondDirectionDepth" : 381 * mm});
        }
        {
            var Q0;
            Q0=qCreatedBy(makeId("Front.planeOp"),FACE);
            var sketch = newSketch(context, id + "F26", { "sketchPlane" : qUnion([Q0])});
            skLineSegment(sketch, "E90", {"start": v(-7321.43, 0) * mm, "end": v(-8418.92, 0) * mm});
            skLineSegment(sketch, "E91", {"start": v(-8418.92, 0) * mm, "end": v(-8418.92, 5486.4) * mm});
            skLineSegment(sketch, "E92", {"start": v(-8418.92, 5486.4) * mm, "end": v(-7331.98, 5486.4) * mm});
            skLineSegment(sketch, "E93", {"start": v(-7331.98, 5486.4) * mm, "end": v(-7321.43, 0) * mm});
            skLineSegment(sketch, "E94", {"start": v(-8418.92, 0) * mm, "end": v(-8803.17, 3637.36) * mm});
            skLineSegment(sketch, "E95", {"start": v(-8803.17, 3637.36) * mm, "end": v(-8418.92, 5486.4) * mm});
            skSolve(sketch);
        }
        {
            var Q0;
            Q0=makeQuery(id+"F26.imprint","IMPRINT",FACE,{"disambiguationData":[TD([[makeQuery(id+"F26.imprint","IMPRINT",EDGE,{"derivedFrom":sQuery(id+"F26.wireOp",EDGE,"E90")}),-1.0]])]});
            extrude(context, id + "F27", {"entities" : qUnion([Q0]), "operationType" : NewBodyOperationType.ADD, "depth" : 5486.4 * mm, "offsetDistance" : 25.4 * mm});
        }
        {
            var Q0;
            Q0 = qSketchRegion(id + "F26", true);
            extrude(context, id + "F28", {"entities" : qUnion([Q0]), "operationType" : NewBodyOperationType.ADD, "depth" : 3657.6 * mm, "offsetDistance" : 25.4 * mm, "hasSecondDirection" : true, "secondDirectionOppositeDirection" : true, "secondDirectionDepth" : 406.4 * mm});
        }
        {
            var Q0;
            Q0=makeQuery(id+"F28.opExtrude","CAP_EDGE",EDGE,{"disambiguationData":[OSD([sQuery(id+"F26.wireOp",EDGE,"E95")])],"isStart":false});
            var Q1;
            Q1=makeQuery(id+"F28.opExtrude","CAP_EDGE",EDGE,{"disambiguationData":[OSD([sQuery(id+"F26.wireOp",EDGE,"E94")])],"isStart":false});
            chamfer(context, id + "F29", {"entities" : qUnion([Q0, Q1]), "chamferType" : ChamferType.TWO_OFFSETS, "width1" : 1828.8 * mm, "oppositeDirection" : false, "width2" : 203.2 * mm, "tangentPropagation" : true});
        }
        {
            var Q0;
            Q0=makeQuery(id+"F28.opExtrude","CAP_EDGE",EDGE,{"disambiguationData":[OSD([sQuery(id+"F26.wireOp",EDGE,"E94")])],"isStart":true});
            var Q1;
            Q1=makeQuery(id+"F28.opExtrude","CAP_EDGE",EDGE,{"disambiguationData":[OSD([sQuery(id+"F26.wireOp",EDGE,"E95")])],"isStart":true});
            chamfer(context, id + "F30", {"entities" : qUnion([Q0, Q1]), "chamferType" : ChamferType.TWO_OFFSETS, "width1" : 203.2 * mm, "oppositeDirection" : false, "width2" : 2235.2 * mm, "tangentPropagation" : true});
        }
        {
            var Q0;
            Q0=qCreatedBy(makeId("Front.planeOp"),FACE);
            var sketch = newSketch(context, id + "F31", { "sketchPlane" : qUnion([Q0])});
            skLineSegment(sketch, "E96", {"start": v(-6726.98, 0) * mm, "end": v(-6163.4, 5486.36) * mm});
            skLineSegment(sketch, "E97", {"start": v(-6163.4, 5486.36) * mm, "end": v(-6707.23, 5486.36) * mm});
            skLineSegment(sketch, "E98", {"start": v(-6707.23, 5486.36) * mm, "end": v(-6726.98, 0) * mm});
            skSolve(sketch);
        }
        {
            var Q0;
            Q0 = qSketchRegion(id + "F31", true);
            extrude(context, id + "F32", {"entities" : qUnion([Q0]), "operationType" : NewBodyOperationType.ADD, "depth" : 5486.4 * mm, "offsetDistance" : 25.4 * mm, "hasSecondDirection" : true, "secondDirectionOppositeDirection" : false, "secondDirectionDepth" : 3149.6 * mm});
        }
        {
            var Q0;
            Q0=makeQuery(id+"F32.opExtrude","CAP_EDGE",EDGE,{"disambiguationData":[OSD([sQuery(id+"F31.wireOp",EDGE,"E96")])],"isStart":true});
            chamfer(context, id + "F33", {"entities" : qUnion([Q0]), "width" : 508 * mm, "tangentPropagation" : true});
        }
        {
            var Q0;
            Q0=qCreatedBy(makeId("Right.planeOp"),FACE);
            var sketch = newSketch(context, id + "F34", { "sketchPlane" : qUnion([Q0])});
            skLineSegment(sketch, "E99", {"start": v(-5557.8, 0) * mm, "end": v(-5737.43, 5483.46) * mm});
            skLineSegment(sketch, "E100", {"start": v(-5557.8, 0) * mm, "end": v(-6536.42, 4153.47) * mm});
            skLineSegment(sketch, "E101", {"start": v(-6536.42, 4153.47) * mm, "end": v(-6175.25, 5483.46) * mm});
            skLineSegment(sketch, "E102", {"start": v(-6175.25, 5483.46) * mm, "end": v(-5737.43, 5483.46) * mm});
            skSolve(sketch);
        }
        {
            var Q0;
            Q0 = qSketchRegion(id + "F34", true);
            extrude(context, id + "F35", {"entities" : qUnion([Q0]), "oppositeDirection" : true, "depth" : 8382 * mm, "offsetDistance" : 25.4 * mm, "hasSecondDirection" : true, "secondDirectionOppositeDirection" : true, "secondDirectionDepth" : 6096 * mm});
        }
        {
            var Q0;
            Q0=makeQuery(id+"F35.opExtrude","CAP_EDGE",EDGE,{"disambiguationData":[OSD([sQuery(id+"F34.wireOp",EDGE,"E100")])],"isStart":false});
            var Q1;
            Q1=makeQuery(id+"F35.opExtrude","CAP_EDGE",EDGE,{"disambiguationData":[OSD([sQuery(id+"F34.wireOp",EDGE,"E101")])],"isStart":false});
            chamfer(context, id + "F36", {"entities" : qUnion([Q0, Q1]), "chamferType" : ChamferType.TWO_OFFSETS, "width1" : 406.4 * mm, "oppositeDirection" : false, "width2" : 1016 * mm, "tangentPropagation" : true});
        }
        {
            var Q0;
            Q0=makeQuery(id+"F35.opExtrude","CAP_EDGE",EDGE,{"disambiguationData":[OSD([sQuery(id+"F34.wireOp",EDGE,"E100")])],"isStart":true});
            var Q1;
            Q1=makeQuery(id+"F35.opExtrude","CAP_EDGE",EDGE,{"disambiguationData":[OSD([sQuery(id+"F34.wireOp",EDGE,"E101")])],"isStart":true});
            chamfer(context, id + "F37", {"entities" : qUnion([Q0, Q1]), "chamferType" : ChamferType.TWO_OFFSETS, "width1" : 1219.2 * mm, "oppositeDirection" : false, "width2" : 406.4 * mm, "tangentPropagation" : true});
        }
    });
